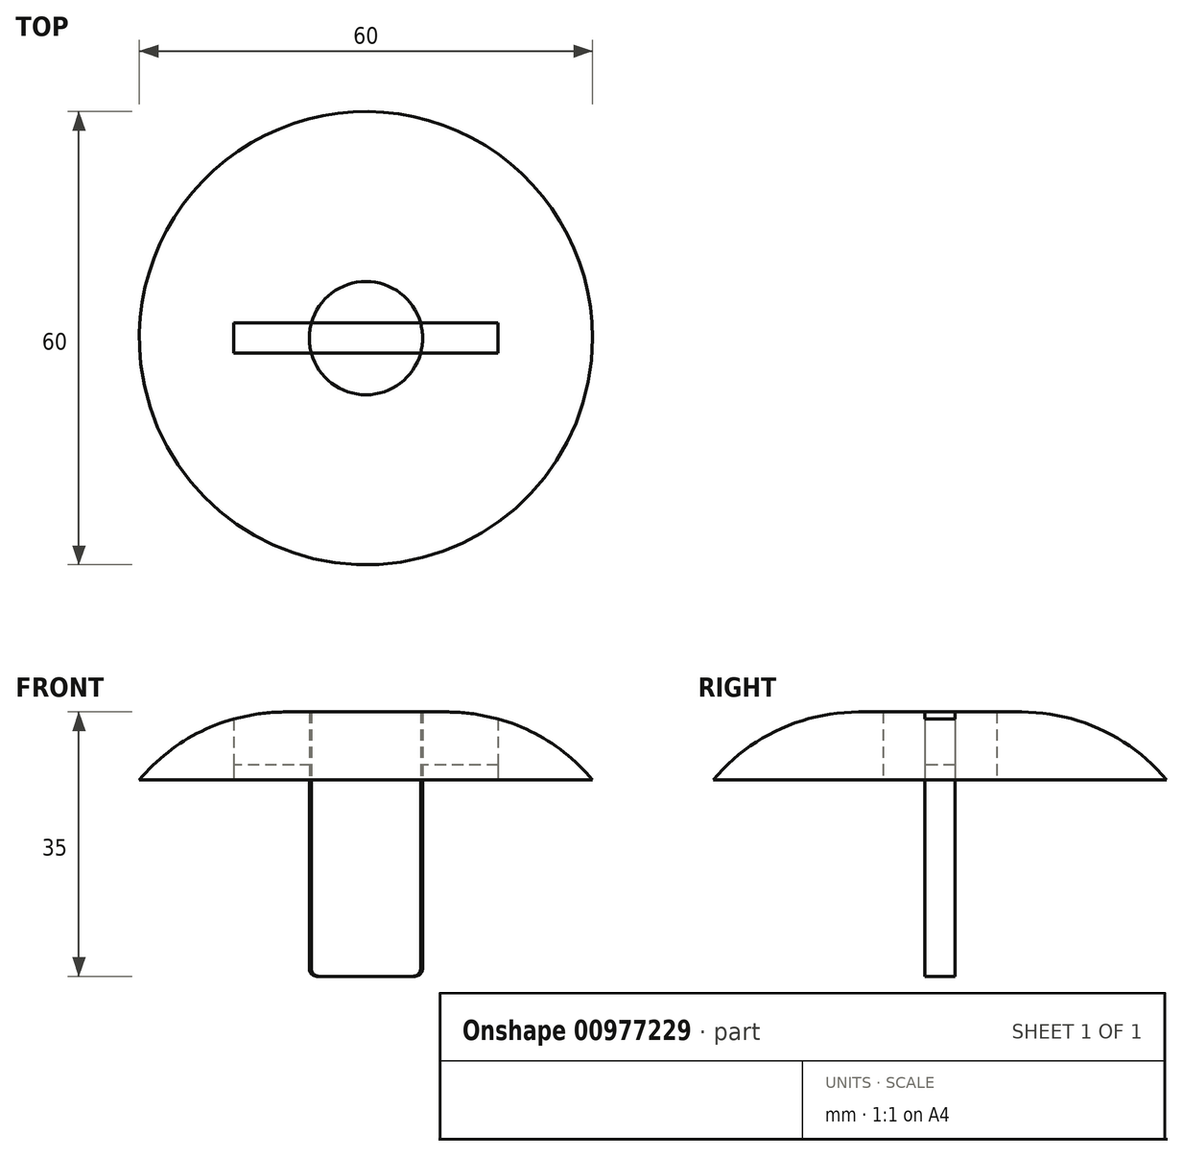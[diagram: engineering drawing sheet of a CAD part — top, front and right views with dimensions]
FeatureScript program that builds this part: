
annotation { "Feature Type Name" : "Feature", "Feature Type Description" : "" }
export const myFeature = defineFeature(function(context is Context, id is Id, definition is map)
    precondition{}
    {
        {
            var Q0;
            Q0=qCreatedBy(makeId("Top.planeOp"),FACE);
            var sketch = newSketch(context, id + "F0", { "sketchPlane" : qUnion([Q0])});
            skCircle(sketch, "E0", {"center": v(0, 0) * mm, "radius": 30 * mm});
            skCircle(sketch, "E1", {"center": v(0, 0) * mm, "radius": 7.5 * mm});
            skLineSegment(sketch, "E2.bottom", {"start": v(17.5, 2) * mm, "end": v(-17.5, 2) * mm});
            skLineSegment(sketch, "E2.top", {"start": v(17.5, -2) * mm, "end": v(-17.5, -2) * mm});
            skLineSegment(sketch, "E2.left", {"start": v(17.5, 2) * mm, "end": v(17.5, -2) * mm});
            skLineSegment(sketch, "E2.right", {"start": v(-17.5, 2) * mm, "end": v(-17.5, -2) * mm});
            skSolve(sketch);
        }
        {
            var Q0;
            Q0=makeQuery(id+"F0.imprint","IMPRINT",FACE,{"disambiguationData":[TD([[makeQuery(id+"F0.imprint","IMPRINT",EDGE,{"derivedFrom":sQuery(id+"F0.wireOp",EDGE,"E1")}),1.0]])]});
            var Q1;
            {var subQ0=sQuery(id+"F0.wireOp",EDGE,"E2.top");var subQ1=sQuery(id+"F0.wireOp",EDGE,"E1");var subQ2=makeQuery(id+"F0.imprint","INTERSECT",VERTEX,{"disambiguationData":[OD(0.0)],"derivedFrom":[subQ1,subQ0]});Q1=makeQuery(id+"F0.imprint","IMPRINT",FACE,{"disambiguationData":[TD([[makeQuery(id+"F0.imprint","IMPRINT",EDGE,{"disambiguationData":[TD([[subQ2,-1.0]])],"derivedFrom":subQ1}),1.0]])]});}
            var Q2;
            {var subQ0=sQuery(id+"F0.wireOp",EDGE,"E2.bottom");var subQ1=sQuery(id+"F0.wireOp",EDGE,"E1");var subQ2=makeQuery(id+"F0.imprint","INTERSECT",VERTEX,{"disambiguationData":[OD(0.0)],"derivedFrom":[subQ1,subQ0]});Q2=makeQuery(id+"F0.imprint","IMPRINT",FACE,{"disambiguationData":[TD([[makeQuery(id+"F0.imprint","IMPRINT",EDGE,{"disambiguationData":[TD([[subQ2,1.0]])],"derivedFrom":subQ1}),1.0]])]});}
            var Q3;
            Q3=sQuery(id+"F0.wireOp",EDGE,"E1");
            extrude(context, id + "F1", {"entities" : qUnion([Q0, Q1, Q2]), "surfaceEntities" : qUnion([Q3]), "depth" : 10 * mm, "offsetDistance" : 25 * mm, "hasSecondDirection" : true, "secondDirectionOppositeDirection" : true, "secondDirectionDepth" : 25 * mm});
        }
        {
            var Q0;
            Q0=makeQuery(id+"F0.imprint","IMPRINT",FACE,{"disambiguationData":[TD([[makeQuery(id+"F0.imprint","IMPRINT",EDGE,{"derivedFrom":sQuery(id+"F0.wireOp",EDGE,"E0")}),1.0]])]});
            var Q1;
            Q1=sQuery(id+"F0.wireOp",EDGE,"E0");
            extrude(context, id + "F2", {"entities" : qUnion([Q0]), "surfaceEntities" : qUnion([Q1]), "depth" : 10 * mm, "offsetDistance" : 25 * mm, "hasSecondDirection" : true, "secondDirectionOppositeDirection" : true, "secondDirectionDepth" : -1 * mm});
        }
        {
            var Q0;
            Q0=makeQuery(id+"F2.opExtrude","CAP_EDGE",EDGE,{"disambiguationData":[OSD([sQuery(id+"F0.wireOp",EDGE,"E0")])],"isStart":false});
            fillet(context, id + "F3", {"entities" : qUnion([Q0]), "radius" : 25 * mm, "tangentPropagation" : true, "allowEdgeOverflow" : false});
        }
        {
            var Q0;
            Q0=makeQuery(id+"F1.opExtrude","CAP_EDGE",EDGE,{"disambiguationData":[OSD([sQuery(id+"F0.wireOp",EDGE,"E1")])],"isStart":true});
            fillet(context, id + "F4", {"entities" : qUnion([Q0]), "radius" : 1 * mm, "tangentPropagation" : true, "allowEdgeOverflow" : false});
        }
        {
            var Q0;
            {var subQ5=sQuery(id+"F0.wireOp",EDGE,"E2.right");Q0=makeQuery(id+"F0.imprint","IMPRINT",FACE,{"disambiguationData":[TD([[makeQuery(id+"F0.imprint","IMPRINT",EDGE,{"derivedFrom":subQ5}),1.0]])]});}
            var Q1;
            {var subQ5=sQuery(id+"F0.wireOp",EDGE,"E2.left");Q1=makeQuery(id+"F0.imprint","IMPRINT",FACE,{"disambiguationData":[TD([[makeQuery(id+"F0.imprint","IMPRINT",EDGE,{"derivedFrom":subQ5}),-1.0]])]});}
            extrude(context, id + "F5", {"entities" : qUnion([Q0, Q1]), "depth" : 3 * mm, "offsetDistance" : 25 * mm, "hasSecondDirection" : true, "secondDirectionOppositeDirection" : true, "secondDirectionDepth" : -1 * mm});
        }
    });
